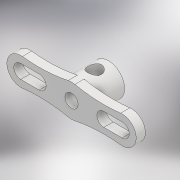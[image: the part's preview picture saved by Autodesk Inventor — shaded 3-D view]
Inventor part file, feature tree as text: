
AUTODESK INVENTOR PART (.ipt)
format: ipt  version: 2018.2 (Build 222227000, 227)  size: 173,568 bytes
history: native  units: mm
features: extrude x3, plane x1, sketch x1
ambient origin geometry x8: Origin, YZ Plane, XZ Plane, XY Plane, X Axis, Y Axis, Z Axis, Center Point
bodies: Solid1 (feature_tree)
feature tree (5):
  extrude  "Extrusion1"  Depth=3.0mm
  extrude  "Extrusion2"  Depth=3.0mm
  extrude  "Extrusion3"  Depth=3.0mm TaperAngle=0.0deg
  plane  "Work Plane1"
  sketch  "Sketch2"  dims[d0=2.85mm d1=7.0mm d6=3.0mm d7=2.0mm d8=0.0mm d9=6.0mm d10=0.0mm d11=3.0mm d12=6.0mm d13=0.0mm d14=30.0mm d15=3.0mm d16=4.0mm d17=7.0mm]
